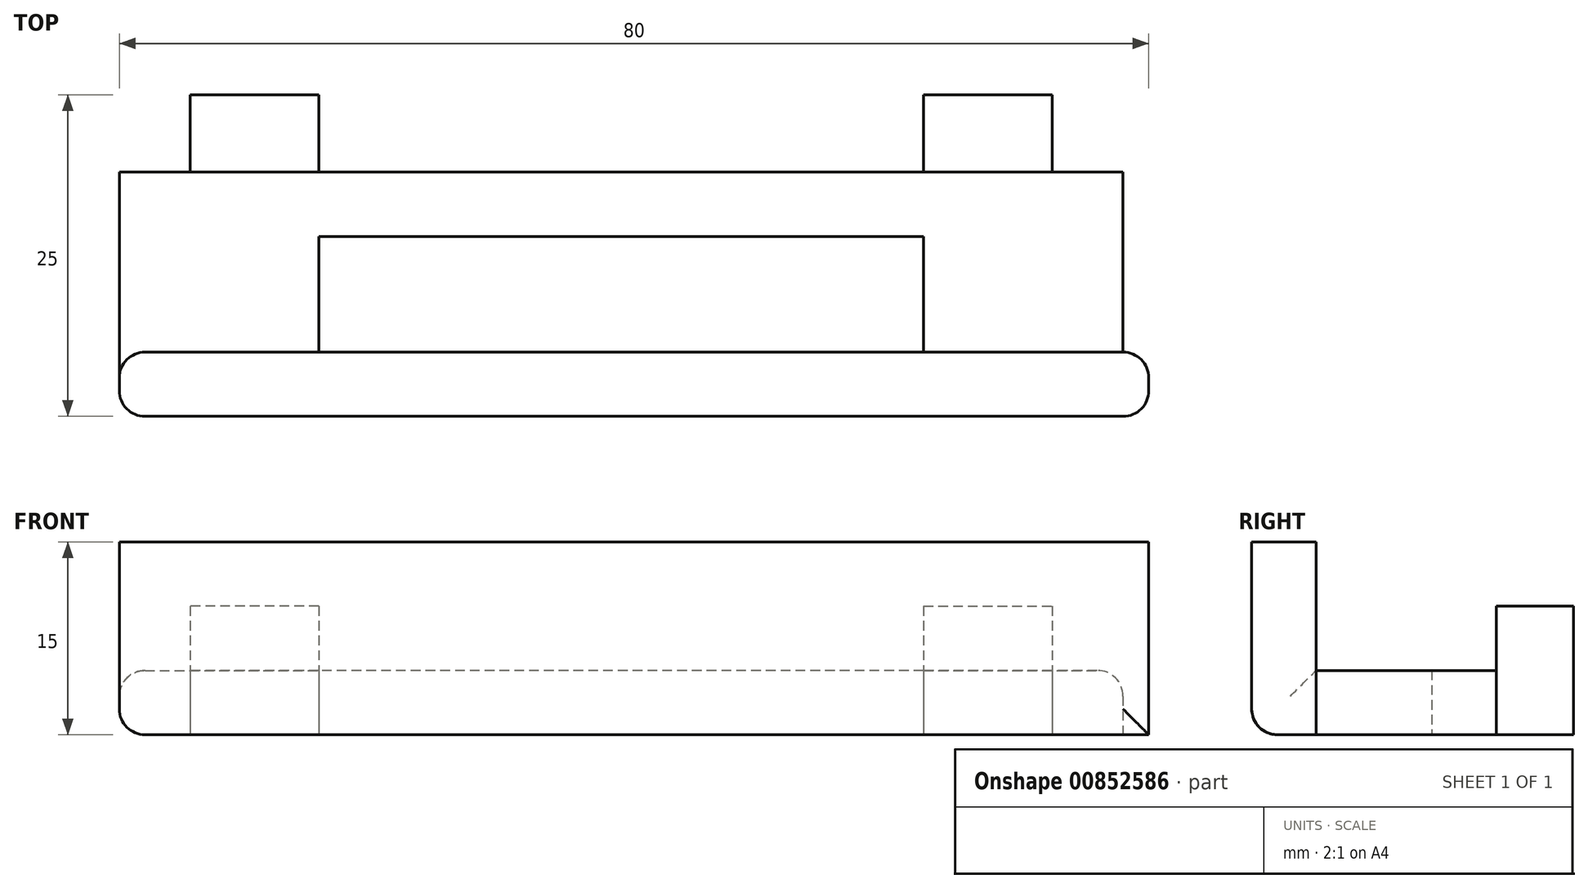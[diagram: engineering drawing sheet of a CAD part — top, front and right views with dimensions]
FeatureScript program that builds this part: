
annotation { "Feature Type Name" : "Feature", "Feature Type Description" : "" }
export const myFeature = defineFeature(function(context is Context, id is Id, definition is map)
    precondition{}
    {
        {
            var Q0;
            Q0=qCreatedBy(makeId("Front.planeOp"),FACE);
            var sketch = newSketch(context, id + "F0", { "sketchPlane" : qUnion([Q0])});
            skLineSegment(sketch, "E0.bottom", {"start": v(-23.5, 5) * mm, "end": v(-33.5, 5) * mm});
            skLineSegment(sketch, "E0.top", {"start": v(-23.5, -5) * mm, "end": v(-33.5, -5) * mm});
            skLineSegment(sketch, "E0.left", {"start": v(-23.5, 5) * mm, "end": v(-23.5, -5) * mm});
            skLineSegment(sketch, "E0.right", {"start": v(-33.5, 5) * mm, "end": v(-33.5, -5) * mm});
            skPoint(sketch, "E0.middle", {"position": v(-28.5, 0) * mm});
            skLineSegment(sketch, "E1.MirrorCS", {"start": v(23.5, 5) * mm, "end": v(23.5, -5) * mm});
            skLineSegment(sketch, "E2.MirrorCS", {"start": v(23.5, 5) * mm, "end": v(33.5, 5) * mm});
            skLineSegment(sketch, "E3.MirrorCS", {"start": v(33.5, 5) * mm, "end": v(33.5, -5) * mm});
            skLineSegment(sketch, "E4.MirrorCS", {"start": v(23.5, -5) * mm, "end": v(33.5, -5) * mm});
            skLineSegment(sketch, "E5.bottom", {"start": v(-33.5, 0) * mm, "end": v(-23.5, 0) * mm});
            skLineSegment(sketch, "E5.top", {"start": v(-33.5, -5) * mm, "end": v(-23.5, -5) * mm});
            skLineSegment(sketch, "E5.left", {"start": v(-33.5, 0) * mm, "end": v(-33.5, -5) * mm});
            skLineSegment(sketch, "E5.right", {"start": v(-23.5, 0) * mm, "end": v(-23.5, -5) * mm});
            skLineSegment(sketch, "E6.bottom", {"start": v(23.5, 0) * mm, "end": v(33.5, 0) * mm});
            skLineSegment(sketch, "E6.left", {"start": v(23.5, 0) * mm, "end": v(23.5, -5) * mm});
            skLineSegment(sketch, "E6.right", {"start": v(33.5, 0) * mm, "end": v(33.5, -5) * mm});
            skSolve(sketch);
        }
        {
            var Q0;
            Q0 = qSketchRegion(id + "F0", true);
            extrude(context, id + "F1", {"entities" : qUnion([Q0]), "depth" : 6 * mm, "offsetDistance" : 25 * mm});
        }
        {
            var Q0;
            Q0=makeQuery(id+"F0.imprint","IMPRINT",FACE,{"disambiguationData":[TD([[makeQuery(id+"F0.imprint","IMPRINT",EDGE,{"derivedFrom":sQuery(id+"F0.wireOp",EDGE,"E6.bottom")}),-1.0]])]});
            var Q1;
            Q1=makeQuery(id+"F0.imprint","IMPRINT",FACE,{"disambiguationData":[TD([[makeQuery(id+"F0.imprint","IMPRINT",EDGE,{"derivedFrom":sQuery(id+"F0.wireOp",EDGE,"E5.bottom")}),-1.0]])]});
            extrude(context, id + "F2", {"entities" : qUnion([Q0, Q1]), "depth" : 20 * mm, "offsetDistance" : 25 * mm});
        }
        {
            var Q0;
            Q0=makeQuery(id+"F1.opExtrude","SWEPT_BODY",BODY,{"disambiguationData":[OSD([sQuery(id+"F0.wireOp",EDGE,"E0.bottom"),sQuery(id+"F0.wireOp",EDGE,"E0.left"),sQuery(id+"F0.wireOp",EDGE,"E0.right"),sQuery(id+"F0.wireOp",EDGE,"E5.top"),sQuery(id+"F0.wireOp",EDGE,"E5.left"),sQuery(id+"F0.wireOp",EDGE,"E5.right")])]});
            var Q1;
            Q1=makeQuery(id+"F1.opExtrude","SWEPT_BODY",BODY,{"disambiguationData":[OSD([sQuery(id+"F0.wireOp",EDGE,"E1.MirrorCS"),sQuery(id+"F0.wireOp",EDGE,"E2.MirrorCS"),sQuery(id+"F0.wireOp",EDGE,"E3.MirrorCS"),sQuery(id+"F0.wireOp",EDGE,"E4.MirrorCS"),sQuery(id+"F0.wireOp",EDGE,"E6.left"),sQuery(id+"F0.wireOp",EDGE,"E6.right")])]});
            var Q2;
            Q2=makeQuery(id+"F2.opExtrude","SWEPT_BODY",BODY,{"disambiguationData":[OSD([sQuery(id+"F0.wireOp",EDGE,"E5.bottom"),sQuery(id+"F0.wireOp",EDGE,"E5.top"),sQuery(id+"F0.wireOp",EDGE,"E5.left"),sQuery(id+"F0.wireOp",EDGE,"E5.right")])]});
            var Q3;
            Q3=makeQuery(id+"F2.opExtrude","SWEPT_BODY",BODY,{"disambiguationData":[OSD([sQuery(id+"F0.wireOp",EDGE,"E6.bottom"),sQuery(id+"F0.wireOp",EDGE,"E4.MirrorCS"),sQuery(id+"F0.wireOp",EDGE,"E6.left"),sQuery(id+"F0.wireOp",EDGE,"E6.right")])]});
            booleanBodies(context, id + "F3", {"operationType" : BooleanOperationType.UNION, "tools" : qUnion([Q0, Q1, Q2, Q3])});
        }
        {
            var Q0;
            Q0=makeQuery(id+"F2.opExtrude","CAP_FACE",FACE,{"disambiguationData":[OSD([sQuery(id+"F0.wireOp",EDGE,"E5.bottom"),sQuery(id+"F0.wireOp",EDGE,"E5.top"),sQuery(id+"F0.wireOp",EDGE,"E5.left"),sQuery(id+"F0.wireOp",EDGE,"E5.right")])],"isStart":false});
            var sketch = newSketch(context, id + "F4", { "sketchPlane" : qUnion([Q0])});
            skLineSegment(sketch, "E7.bottom", {"start": v(-39, -5) * mm, "end": v(41, -5) * mm});
            skLineSegment(sketch, "E7.top", {"start": v(-39, 10) * mm, "end": v(41, 10) * mm});
            skLineSegment(sketch, "E7.left", {"start": v(-39, -5) * mm, "end": v(-39, 10) * mm});
            skLineSegment(sketch, "E7.right", {"start": v(41, -5) * mm, "end": v(41, 10) * mm});
            skSolve(sketch);
        }
        {
            var Q0;
            Q0 = qSketchRegion(id + "F4", true);
            extrude(context, id + "F5", {"entities" : qUnion([Q0]), "depth" : 5 * mm, "offsetDistance" : 25 * mm});
        }
        {
            var Q0;
            {var subQ0=sQuery(id+"F0.wireOp",EDGE,"E6.right");Q0=makeQuery(id+"F3.opBoolean","MERGE",FACE,{"derivedFrom":[makeQuery(id+"F1.opExtrude","SWEPT_FACE",FACE,{"disambiguationData":[OSD([sQuery(id+"F0.wireOp",EDGE,"E3.MirrorCS"),subQ0])]}),makeQuery(id+"F2.opExtrude","SWEPT_FACE",FACE,{"disambiguationData":[OSD([subQ0])]})]});}
            var sketch = newSketch(context, id + "F6", { "sketchPlane" : qUnion([Q0])});
            skLineSegment(sketch, "E8.bottom", {"start": v(-20, 0) * mm, "end": v(-6, 0) * mm});
            skLineSegment(sketch, "E8.top", {"start": v(-20, -5) * mm, "end": v(-6, -5) * mm});
            skLineSegment(sketch, "E8.left", {"start": v(-20, 0) * mm, "end": v(-20, -5) * mm});
            skLineSegment(sketch, "E8.right", {"start": v(-6, 0) * mm, "end": v(-6, -5) * mm});
            skSolve(sketch);
        }
        {
            var Q0;
            Q0 = qSketchRegion(id + "F6", true);
            extrude(context, id + "F7", {"entities" : qUnion([Q0]), "depth" : 5.5 * mm, "offsetDistance" : 25 * mm});
        }
        {
            var Q0;
            Q0=makeQuery(id+"F7.opExtrude","SWEPT_BODY",BODY,{"disambiguationData":[OSD([sQuery(id+"F6.wireOp",EDGE,"E8.bottom"),sQuery(id+"F6.wireOp",EDGE,"E8.top"),sQuery(id+"F6.wireOp",EDGE,"E8.left"),sQuery(id+"F6.wireOp",EDGE,"E8.right")])]});
            var Q1;
            Q1=qCreatedBy(makeId("Right.planeOp"),FACE);
            mirror(context, id + "F8", {"entities" : qUnion([Q0]), "mirrorPlane" : qUnion([Q1])});
        }
        {
            var Q0;
            Q0=makeQuery(id+"F1.opExtrude","SWEPT_BODY",BODY,{"disambiguationData":[OSD([sQuery(id+"F0.wireOp",EDGE,"E0.bottom"),sQuery(id+"F0.wireOp",EDGE,"E0.left"),sQuery(id+"F0.wireOp",EDGE,"E0.right"),sQuery(id+"F0.wireOp",EDGE,"E5.top"),sQuery(id+"F0.wireOp",EDGE,"E5.left"),sQuery(id+"F0.wireOp",EDGE,"E5.right")])]});
            var Q1;
            Q1=makeQuery(id+"F1.opExtrude","SWEPT_BODY",BODY,{"disambiguationData":[OSD([sQuery(id+"F0.wireOp",EDGE,"E1.MirrorCS"),sQuery(id+"F0.wireOp",EDGE,"E2.MirrorCS"),sQuery(id+"F0.wireOp",EDGE,"E3.MirrorCS"),sQuery(id+"F0.wireOp",EDGE,"E4.MirrorCS"),sQuery(id+"F0.wireOp",EDGE,"E6.left"),sQuery(id+"F0.wireOp",EDGE,"E6.right")])]});
            var Q2;
            Q2=makeQuery(id+"F5.opExtrude","SWEPT_BODY",BODY,{"disambiguationData":[OSD([sQuery(id+"F4.wireOp",EDGE,"E7.bottom"),sQuery(id+"F4.wireOp",EDGE,"E7.top"),sQuery(id+"F4.wireOp",EDGE,"E7.left"),sQuery(id+"F4.wireOp",EDGE,"E7.right")])]});
            var Q3;
            Q3=makeQuery(id+"F8.opPattern","COPY",BODY,{"derivedFrom":makeQuery(id+"F7.opExtrude","SWEPT_BODY",BODY,{"disambiguationData":[OSD([sQuery(id+"F6.wireOp",EDGE,"E8.bottom"),sQuery(id+"F6.wireOp",EDGE,"E8.top"),sQuery(id+"F6.wireOp",EDGE,"E8.left"),sQuery(id+"F6.wireOp",EDGE,"E8.right")])]}),"instanceName":"1"});
            var Q4;
            Q4=makeQuery(id+"F7.opExtrude","SWEPT_BODY",BODY,{"disambiguationData":[OSD([sQuery(id+"F6.wireOp",EDGE,"E8.bottom"),sQuery(id+"F6.wireOp",EDGE,"E8.top"),sQuery(id+"F6.wireOp",EDGE,"E8.left"),sQuery(id+"F6.wireOp",EDGE,"E8.right")])]});
            booleanBodies(context, id + "F9", {"operationType" : BooleanOperationType.UNION, "tools" : qUnion([Q0, Q1, Q2, Q3, Q4])});
        }
        {
            var Q0;
            Q0=makeQuery(id+"F8.opPattern","COPY",EDGE,{"derivedFrom":makeQuery(id+"F7.opExtrude","CAP_EDGE",EDGE,{"disambiguationData":[OSD([sQuery(id+"F6.wireOp",EDGE,"E8.bottom")])],"isStart":false}),"instanceName":"1"});
            var Q1;
            Q1=makeQuery(id+"F9.opBoolean","MERGE",EDGE,{"derivedFrom":[makeQuery(id+"F5.opExtrude","SWEPT_EDGE",EDGE,{"disambiguationData":[OSD([sQuery(id+"F4.wireOp",EDGE,"E7.bottom"),sQuery(id+"F4.wireOp",EDGE,"E7.left")])]}),makeQuery(id+"F8.opPattern","COPY",EDGE,{"derivedFrom":makeQuery(id+"F7.opExtrude","CAP_EDGE",EDGE,{"disambiguationData":[OSD([sQuery(id+"F6.wireOp",EDGE,"E8.top")])],"isStart":false}),"instanceName":"1"})]});
            var Q2;
            Q2=makeQuery(id+"F7.opExtrude","CAP_EDGE",EDGE,{"disambiguationData":[OSD([sQuery(id+"F6.wireOp",EDGE,"E8.bottom")])],"isStart":false});
            var Q3;
            Q3=makeQuery(id+"F9.opBoolean","MERGE",EDGE,{"derivedFrom":[makeQuery(id+"F5.opExtrude","SWEPT_EDGE",EDGE,{"disambiguationData":[OSD([sQuery(id+"F4.wireOp",EDGE,"E7.bottom"),sQuery(id+"F4.wireOp",EDGE,"E7.right")])]}),makeQuery(id+"F7.opExtrude","CAP_EDGE",EDGE,{"disambiguationData":[OSD([sQuery(id+"F6.wireOp",EDGE,"E8.top")])],"isStart":false})]});
            var Q4;
            Q4=makeQuery(id+"F5.opExtrude","CAP_EDGE",EDGE,{"disambiguationData":[OSD([sQuery(id+"F4.wireOp",EDGE,"E7.right")])],"isStart":true});
            var Q5;
            Q5=makeQuery(id+"F5.opExtrude","CAP_EDGE",EDGE,{"disambiguationData":[OSD([sQuery(id+"F4.wireOp",EDGE,"E7.left")])],"isStart":true});
            var Q6;
            Q6=makeQuery(id+"F5.opExtrude","CAP_EDGE",EDGE,{"disambiguationData":[OSD([sQuery(id+"F4.wireOp",EDGE,"E7.left")])],"isStart":false});
            var Q7;
            Q7=makeQuery(id+"F5.opExtrude","CAP_EDGE",EDGE,{"disambiguationData":[OSD([sQuery(id+"F4.wireOp",EDGE,"E7.right")])],"isStart":false});
            var Q8;
            Q8=makeQuery(id+"F5.opExtrude","CAP_EDGE",EDGE,{"disambiguationData":[OSD([sQuery(id+"F4.wireOp",EDGE,"E7.bottom")])],"isStart":false});
            fillet(context, id + "F10", {"entities" : qUnion([Q0, Q1, Q2, Q3, Q4, Q5, Q6, Q7, Q8]), "radius" : 2 * mm, "tangentPropagation" : true, "allowEdgeOverflow" : false});
        }
        {
            var Q0;
            {var subQ0=sQuery(id+"F0.wireOp",EDGE,"E5.right");Q0=makeQuery(id+"F3.opBoolean","MERGE",FACE,{"derivedFrom":[makeQuery(id+"F1.opExtrude","SWEPT_FACE",FACE,{"disambiguationData":[OSD([sQuery(id+"F0.wireOp",EDGE,"E0.left"),subQ0])]}),makeQuery(id+"F2.opExtrude","SWEPT_FACE",FACE,{"disambiguationData":[OSD([subQ0])]})]});}
            var sketch = newSketch(context, id + "F11", { "sketchPlane" : qUnion([Q0])});
            skLineSegment(sketch, "E9.bottom", {"start": v(-6, 0) * mm, "end": v(-11, 0) * mm});
            skLineSegment(sketch, "E9.top", {"start": v(-6, -5) * mm, "end": v(-11, -5) * mm});
            skLineSegment(sketch, "E9.left", {"start": v(-6, 0) * mm, "end": v(-6, -5) * mm});
            skLineSegment(sketch, "E9.right", {"start": v(-11, 0) * mm, "end": v(-11, -5) * mm});
            skSolve(sketch);
        }
        {
            var Q0;
            Q0 = qSketchRegion(id + "F11", true);
            extrude(context, id + "F12", {"entities" : qUnion([Q0]), "operationType" : NewBodyOperationType.ADD, "endBound" : BoundingType.UP_TO_NEXT, "depth" : 25 * mm, "offsetDistance" : 25 * mm});
        }
    });
